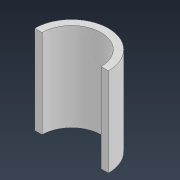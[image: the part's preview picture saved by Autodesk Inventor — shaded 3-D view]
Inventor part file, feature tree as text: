
AUTODESK INVENTOR PART (.ipt)
format: ipt  version: 2022 (Build 260153000, 153)  size: 87,040 bytes
history: native  units: mm
features: extrude x1, sketch x1
ambient origin geometry x8: Origin, YZ Plane, XZ Plane, XY Plane, X Axis, Y Axis, Z Axis, Center Point
bodies: Solid1 (feature_tree)
feature tree (2):
  extrude  "Extrusion1"  Depth=30.0mm
  sketch  "Sketch1"  dims[d0=20.0mm d1=25.0mm d2=30.0mm d3=0.0mm]
